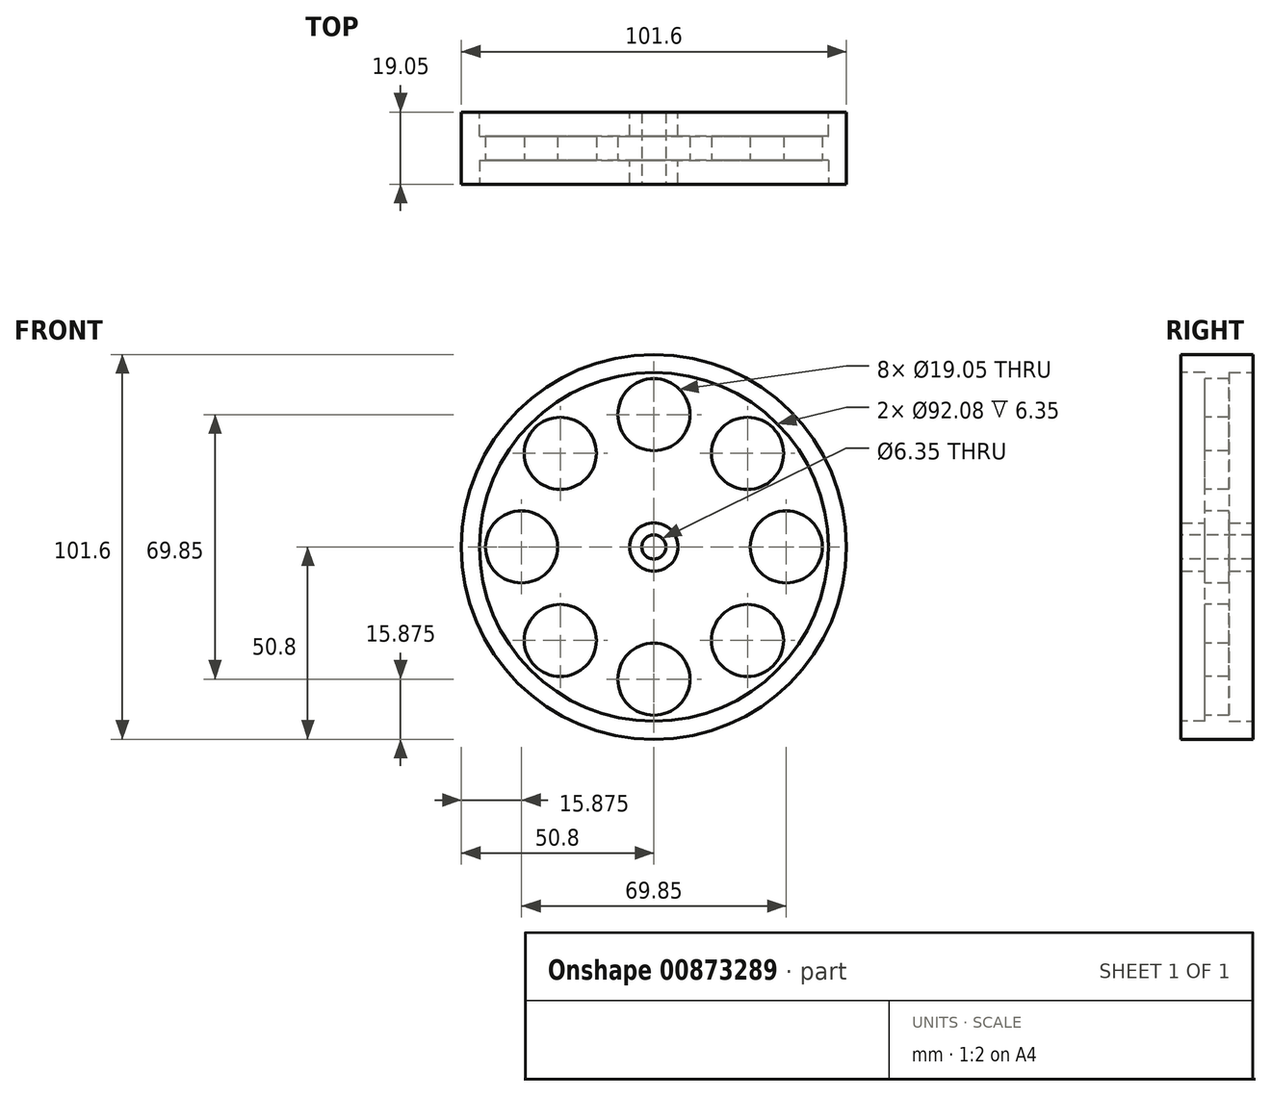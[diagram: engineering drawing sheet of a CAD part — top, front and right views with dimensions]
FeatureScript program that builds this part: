
annotation { "Feature Type Name" : "Feature", "Feature Type Description" : "" }
export const myFeature = defineFeature(function(context is Context, id is Id, definition is map)
    precondition{}
    {
        {
            var Q0;
            Q0=qCreatedBy(makeId("Front.planeOp"),FACE);
            var sketch = newSketch(context, id + "F0", { "sketchPlane" : qUnion([Q0])});
            skCircle(sketch, "E0", {"center": v(0, 0) * mm, "radius": 50.8 * mm});
            skSolve(sketch);
        }
        {
            var Q0;
            Q0 = qSketchRegion(id + "F0", true);
            extrude(context, id + "F1", {"entities" : qUnion([Q0]), "depth" : 19.05 * mm, "offsetDistance" : 25.4 * mm});
        }
        {
            var Q0;
            Q0=makeQuery(id+"F1.opExtrude","CAP_FACE",FACE,{"disambiguationData":[OSD([sQuery(id+"F0.wireOp",EDGE,"E0")])],"isStart":false});
            var sketch = newSketch(context, id + "F2", { "sketchPlane" : qUnion([Q0])});
            skCircle(sketch, "E1", {"center": v(0, 0) * mm, "radius": 3.18 * mm});
            skSolve(sketch);
        }
        {
            var Q0;
            Q0=makeQuery(id+"F2.imprint","IMPRINT",FACE,{"disambiguationData":[TD([[makeQuery(id+"F2.imprint","IMPRINT",EDGE,{"derivedFrom":sQuery(id+"F2.wireOp",EDGE,"E1")}),1.0]])]});
            extrude(context, id + "F3", {"entities" : qUnion([Q0]), "operationType" : NewBodyOperationType.REMOVE, "endBound" : BoundingType.THROUGH_ALL, "oppositeDirection" : true, "depth" : 25.4 * mm, "offsetDistance" : 25.4 * mm});
        }
        {
            var Q0;
            Q0=makeQuery(id+"F1.opExtrude","CAP_FACE",FACE,{"disambiguationData":[OSD([sQuery(id+"F0.wireOp",EDGE,"E0")])],"isStart":false});
            var sketch = newSketch(context, id + "F4", { "sketchPlane" : qUnion([Q0])});
            skCircle(sketch, "E2", {"center": v(0, 34.93) * mm, "radius": 9.53 * mm});
            skCircle(sketch, "E3", {"center": v(0, 0) * mm, "radius": 34.93 * mm, "construction": true});
            skCircle(sketch, "E4.1.0", {"center": v(-24.7, 24.7) * mm, "radius": 9.53 * mm});
            skCircle(sketch, "E4.2.0", {"center": v(-34.93, 0) * mm, "radius": 9.52 * mm});
            skCircle(sketch, "E4.3.0", {"center": v(-24.7, -24.7) * mm, "radius": 9.53 * mm});
            skCircle(sketch, "E4.4.0", {"center": v(0, -34.93) * mm, "radius": 9.53 * mm});
            skCircle(sketch, "E4.5.0", {"center": v(24.7, -24.7) * mm, "radius": 9.53 * mm});
            skCircle(sketch, "E5.1.6.0", {"center": v(34.93, 0) * mm, "radius": 9.53 * mm});
            skCircle(sketch, "E5.1.7.0", {"center": v(24.7, 24.7) * mm, "radius": 9.53 * mm});
            skSolve(sketch);
        }
        {
            var Q0;
            Q0=makeQuery(id+"F4.imprint","IMPRINT",FACE,{"disambiguationData":[TD([[makeQuery(id+"F4.imprint","IMPRINT",EDGE,{"derivedFrom":sQuery(id+"F4.wireOp",EDGE,"E4.1.0")}),1.0]])]});
            var Q1;
            Q1=makeQuery(id+"F4.imprint","IMPRINT",FACE,{"disambiguationData":[TD([[makeQuery(id+"F4.imprint","IMPRINT",EDGE,{"derivedFrom":sQuery(id+"F4.wireOp",EDGE,"E2")}),1.0]])]});
            var Q2;
            Q2=makeQuery(id+"F4.imprint","IMPRINT",FACE,{"disambiguationData":[TD([[makeQuery(id+"F4.imprint","IMPRINT",EDGE,{"derivedFrom":sQuery(id+"F4.wireOp",EDGE,"E4.5.0")}),1.0]])]});
            var Q3;
            Q3=makeQuery(id+"F4.imprint","IMPRINT",FACE,{"disambiguationData":[TD([[makeQuery(id+"F4.imprint","IMPRINT",EDGE,{"derivedFrom":sQuery(id+"F4.wireOp",EDGE,"E4.4.0")}),1.0]])]});
            var Q4;
            Q4=makeQuery(id+"F4.imprint","IMPRINT",FACE,{"disambiguationData":[TD([[makeQuery(id+"F4.imprint","IMPRINT",EDGE,{"derivedFrom":sQuery(id+"F4.wireOp",EDGE,"E4.3.0")}),1.0]])]});
            var Q5;
            Q5=makeQuery(id+"F4.imprint","IMPRINT",FACE,{"disambiguationData":[TD([[makeQuery(id+"F4.imprint","IMPRINT",EDGE,{"derivedFrom":sQuery(id+"F4.wireOp",EDGE,"E4.2.0")}),1.0]])]});
            var Q6;
            Q6=makeQuery(id+"F4.imprint","IMPRINT",FACE,{"disambiguationData":[TD([[makeQuery(id+"F4.imprint","IMPRINT",EDGE,{"derivedFrom":sQuery(id+"F4.wireOp",EDGE,"E5.1.7.0")}),1.0]])]});
            var Q7;
            Q7=makeQuery(id+"F4.imprint","IMPRINT",FACE,{"disambiguationData":[TD([[makeQuery(id+"F4.imprint","IMPRINT",EDGE,{"derivedFrom":sQuery(id+"F4.wireOp",EDGE,"E5.1.6.0")}),1.0]])]});
            extrude(context, id + "F5", {"entities" : qUnion([Q0, Q1, Q2, Q3, Q4, Q5, Q6, Q7]), "operationType" : NewBodyOperationType.REMOVE, "endBound" : BoundingType.THROUGH_ALL, "oppositeDirection" : true, "depth" : 25.4 * mm, "offsetDistance" : 25.4 * mm});
        }
        {
            var Q0;
            Q0=makeQuery(id+"F1.opExtrude","CAP_FACE",FACE,{"disambiguationData":[OSD([sQuery(id+"F0.wireOp",EDGE,"E0")])],"isStart":false});
            var sketch = newSketch(context, id + "F6", { "sketchPlane" : qUnion([Q0])});
            skCircle(sketch, "E6", {"center": v(0, 0) * mm, "radius": 46.04 * mm});
            skSolve(sketch);
        }
        {
            var Q0;
            Q0=makeQuery(id+"F6.imprint","IMPRINT",FACE,{"disambiguationData":[TD([[makeQuery(id+"F6.imprint","IMPRINT",EDGE,{"derivedFrom":sQuery(id+"F6.wireOp",EDGE,"E6")}),1.0]])]});
            extrude(context, id + "F7", {"entities" : qUnion([Q0]), "operationType" : NewBodyOperationType.REMOVE, "oppositeDirection" : true, "depth" : 6.35 * mm, "offsetDistance" : 25.4 * mm});
        }
        {
            var Q0;
            Q0=makeQuery(id+"F1.opExtrude","CAP_FACE",FACE,{"disambiguationData":[OSD([sQuery(id+"F0.wireOp",EDGE,"E0")])],"isStart":true});
            var sketch = newSketch(context, id + "F8", { "sketchPlane" : qUnion([Q0])});
            skCircle(sketch, "E7.0", {"center": v(0, 0) * mm, "radius": 46.04 * mm});
            skSolve(sketch);
        }
        {
            var Q0;
            Q0=makeQuery(id+"F8.imprint","IMPRINT",FACE,{"disambiguationData":[TD([[makeQuery(id+"F8.imprint","IMPRINT",EDGE,{"derivedFrom":sQuery(id+"F8.wireOp",EDGE,"E7.0")}),1.0]])]});
            extrude(context, id + "F9", {"entities" : qUnion([Q0]), "operationType" : NewBodyOperationType.REMOVE, "oppositeDirection" : true, "depth" : 6.35 * mm, "offsetDistance" : 25.4 * mm});
        }
        {
            var Q0;
            Q0=makeQuery(id+"F7.boolean.opBoolean","COPY",FACE,{"derivedFrom":makeQuery(id+"F7.opExtrude","CAP_FACE",FACE,{"disambiguationData":[OSD([sQuery(id+"F2.wireOp",EDGE,"E1"),sQuery(id+"F4.wireOp",EDGE,"E2"),sQuery(id+"F4.wireOp",EDGE,"E4.1.0"),sQuery(id+"F4.wireOp",EDGE,"E4.2.0"),sQuery(id+"F4.wireOp",EDGE,"E4.3.0"),sQuery(id+"F4.wireOp",EDGE,"E4.4.0"),sQuery(id+"F4.wireOp",EDGE,"E4.5.0"),sQuery(id+"F4.wireOp",EDGE,"E5.1.6.0"),sQuery(id+"F4.wireOp",EDGE,"E5.1.7.0"),sQuery(id+"F6.wireOp",EDGE,"E6")])],"isStart":false})});
            var sketch = newSketch(context, id + "F10", { "sketchPlane" : qUnion([Q0])});
            skCircle(sketch, "E8", {"center": v(0, 0) * mm, "radius": 6.35 * mm});
            skSolve(sketch);
        }
        {
            var Q0;
            Q0=makeQuery(id+"F10.imprint","IMPRINT",FACE,{"disambiguationData":[TD([[makeQuery(id+"F10.imprint","IMPRINT",EDGE,{"derivedFrom":sQuery(id+"F10.wireOp",EDGE,"E8")}),1.0]])]});
            var Q1;
            Q1=makeQuery(id+"F1.opExtrude","CAP_FACE",FACE,{"disambiguationData":[OSD([sQuery(id+"F0.wireOp",EDGE,"E0")])],"isStart":false});
            var Q2;
            Q2=makeQuery(id+"F1.opExtrude","CAP_FACE",FACE,{"disambiguationData":[OSD([sQuery(id+"F0.wireOp",EDGE,"E0")])],"isStart":true});
            extrude(context, id + "F11", {"entities" : qUnion([Q0]), "operationType" : NewBodyOperationType.ADD, "endBound" : BoundingType.UP_TO_SURFACE, "depth" : 25.4 * mm, "endBoundEntityFace" : qUnion([Q1]), "offsetDistance" : 25.4 * mm, "hasSecondDirection" : true, "secondDirectionBound" : SecondDirectionBoundingType.UP_TO_SURFACE, "secondDirectionOppositeDirection" : true, "secondDirectionDepth" : 25.4 * mm, "secondDirectionBoundEntityFace" : qUnion([Q2])});
        }
    });
